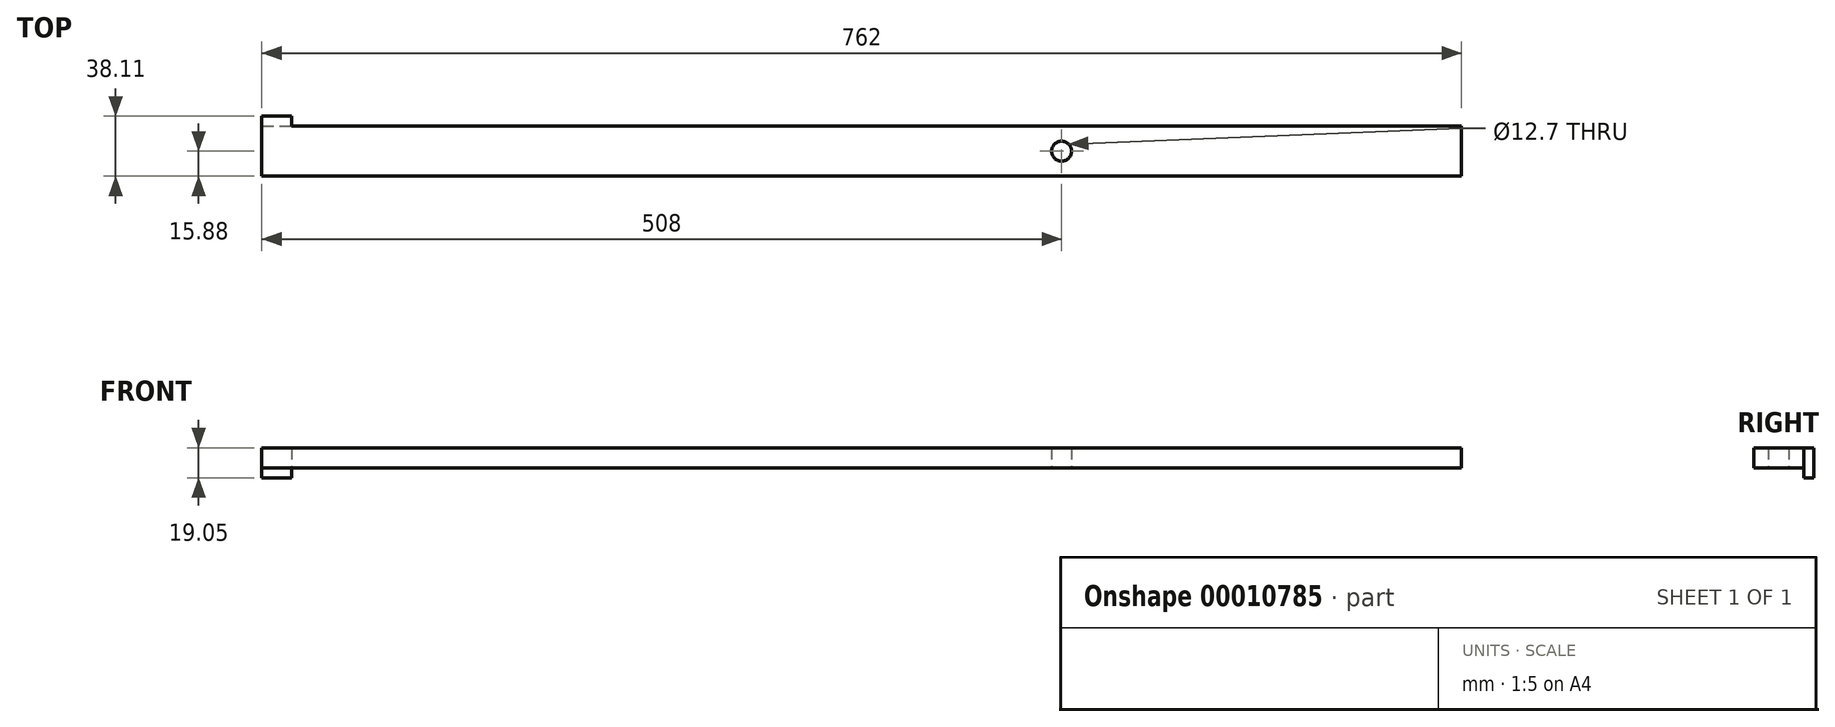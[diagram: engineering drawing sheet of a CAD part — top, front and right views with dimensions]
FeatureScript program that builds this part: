
annotation { "Feature Type Name" : "Feature", "Feature Type Description" : "" }
export const myFeature = defineFeature(function(context is Context, id is Id, definition is map)
    precondition{}
    {
        {
            var Q0;
            Q0=qCreatedBy(makeId("Top.planeOp"),FACE);
            var sketch = newSketch(context, id + "F0", { "sketchPlane" : qUnion([Q0])});
            skCircle(sketch, "E0", {"center": v(0, 0) * mm, "radius": 6.35 * mm});
            skLineSegment(sketch, "E1.bottom", {"start": v(-508, 15.88) * mm, "end": v(254, 15.88) * mm});
            skLineSegment(sketch, "E1.top", {"start": v(-508, -15.88) * mm, "end": v(254, -15.88) * mm});
            skLineSegment(sketch, "E1.left", {"start": v(-508, 15.88) * mm, "end": v(-508, -15.88) * mm});
            skLineSegment(sketch, "E1.right", {"start": v(254, 15.88) * mm, "end": v(254, -15.88) * mm});
            skSolve(sketch);
        }
        {
            var Q0;
            Q0 = qSketchRegion(id + "F0", true);
            extrude(context, id + "F1", {"entities" : qUnion([Q0]), "depth" : 12.7 * mm});
        }
        {
            var Q0;
            Q0=makeQuery(id+"F1.opExtrude","SWEPT_FACE",FACE,{"disambiguationData":[OSD([sQuery(id+"F0.wireOp",EDGE,"E1.bottom")])]});
            var sketch = newSketch(context, id + "F2", { "sketchPlane" : qUnion([Q0])});
            skLineSegment(sketch, "E2.bottom", {"start": v(508, 12.7) * mm, "end": v(488.95, 12.7) * mm});
            skLineSegment(sketch, "E2.top", {"start": v(508, -6.35) * mm, "end": v(488.95, -6.35) * mm});
            skLineSegment(sketch, "E2.left", {"start": v(508, 12.7) * mm, "end": v(508, -6.35) * mm});
            skLineSegment(sketch, "E2.right", {"start": v(488.95, 12.7) * mm, "end": v(488.95, -6.35) * mm});
            skSolve(sketch);
        }
        {
            var Q0;
            Q0 = qSketchRegion(id + "F2", true);
            extrude(context, id + "F3", {"entities" : qUnion([Q0]), "operationType" : NewBodyOperationType.ADD, "depth" : 6.35 * mm});
        }
    });
